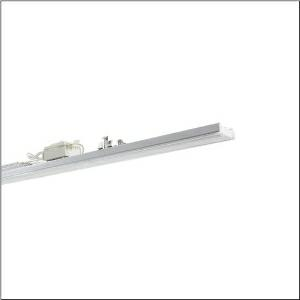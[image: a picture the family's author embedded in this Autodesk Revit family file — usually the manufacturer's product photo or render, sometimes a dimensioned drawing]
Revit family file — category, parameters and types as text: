
# Revit family: licross_21_recessed_mo_52te12dv3dxg
name_source: partatom
category: Lighting Fixtures
units: mm (PartAtom-declared; Revit-internal decimal feet)

## family parameters
Cut with Voids When Loaded = No
Host = Face
Light Source = No
Part Type = Normal
Room Calculation Point = No
Round Connector Dimension = Use Diameter
Shared = No

## types (1)
- --- (1 x LED, 13000 lm, 76.1 W, 3000K)
    Apparent Load = 76 VA
    CIE Flux Codes = 72 92 99 100 100
    Color Rendering = 80
    Color Temperature = 3000K
    Default Elevation = 1800 mm
    Description = Licross 21 Recessed MO, luminaire insert, of sheet steel, galvanised, coil coated, white, length: 2.250mm, width: 66mm, height: 67mm, LED rated luminous flux: 13.000lm, light colour: 830, SDCM (Standard Deviation of Colour Matching)MacAdam ≤ 3 SDCM (initial), control gear: DALI 2, with plug, 5-pole, with phase selection, mains connection: 220..240V, AC, 50/60Hz, rated input power: 76W, internal wiring halogen-free, primary optical cover: cover, of PMMA, light emission: direct distribution, primary light characteristic: symmetric, protection rating (complete): IP54, insulation class (complete): insulation class I (protective earthing), certification: CE, ENEC, VDE, UKCA, protection symbol: D if used in an environment with non-conductive dust loads with corresponding accessories, impact resistance: IK06, permissible ambient temperature for indoor applications: -25..+35°C, corresponds to IFS (International Featured Standards) requirements for safety and quality in the food industry, reducing of maximum allowable ambient temperature of 5°C with ceiling mounting, LABS conformity tested according to VDMA 24364:2018-05, The light source and the operating device comply with the requirements of the Ecodesign Regulation (EU) 2019/2020 and are replaceable in accordance with this regulation, packaging unit: 1 piece
    Height = 58 mm
    Lamp = 1 x LED
    Lamp Light Flux = 13000 lm
    Lamp Power = 76.1 W
    Lamp count = 1
    Length = 2250 mm
    Luminous efficacy = 171 lm/W
    Manufacturer = Siteco
    ModVariant = No
    Model = 52TE12DV3DXG
    Mounting Place = Ceiling
    Mounting Type = Pendant
    Number of Poles = 1
    OnlyDefault = Yes
    Power Factor = 1
    Product Name = Licross 21 Recessed MO
    Product group = luminaire insert | ceiling pendant
    ProductGroupID = 901
    Protection Class = Protection class I
    Protection Degree = IP 54
    RLX_Detail_Level = 1
    RLX_Emergency_Light_Flux = 0 lm
    RLX_Emergency_Type = 0
    RLX_Emergency_Type_DB = No
    RlxData = <blob elided: 29953 chars, md5=4baeba39>
    Socket = socket
    Standby Power = 0 W
    System Light Flux = 13000 lm
    System Power = 76 W
    Type Comments = factory setting: luminous flux: 100 % | dim-lin: 254 | 347 mA
    Type Image = l_1296930.jpg
    URL = http://relux.com
    VarID = @adj_039179
    Voltage = 0 V
    Weight = 0.00 kg
    Width = 66 mm

## geometry (parser evidence)
native form markers: Blend x4, Sweep x10
no freeform markers — native parametric forms only
